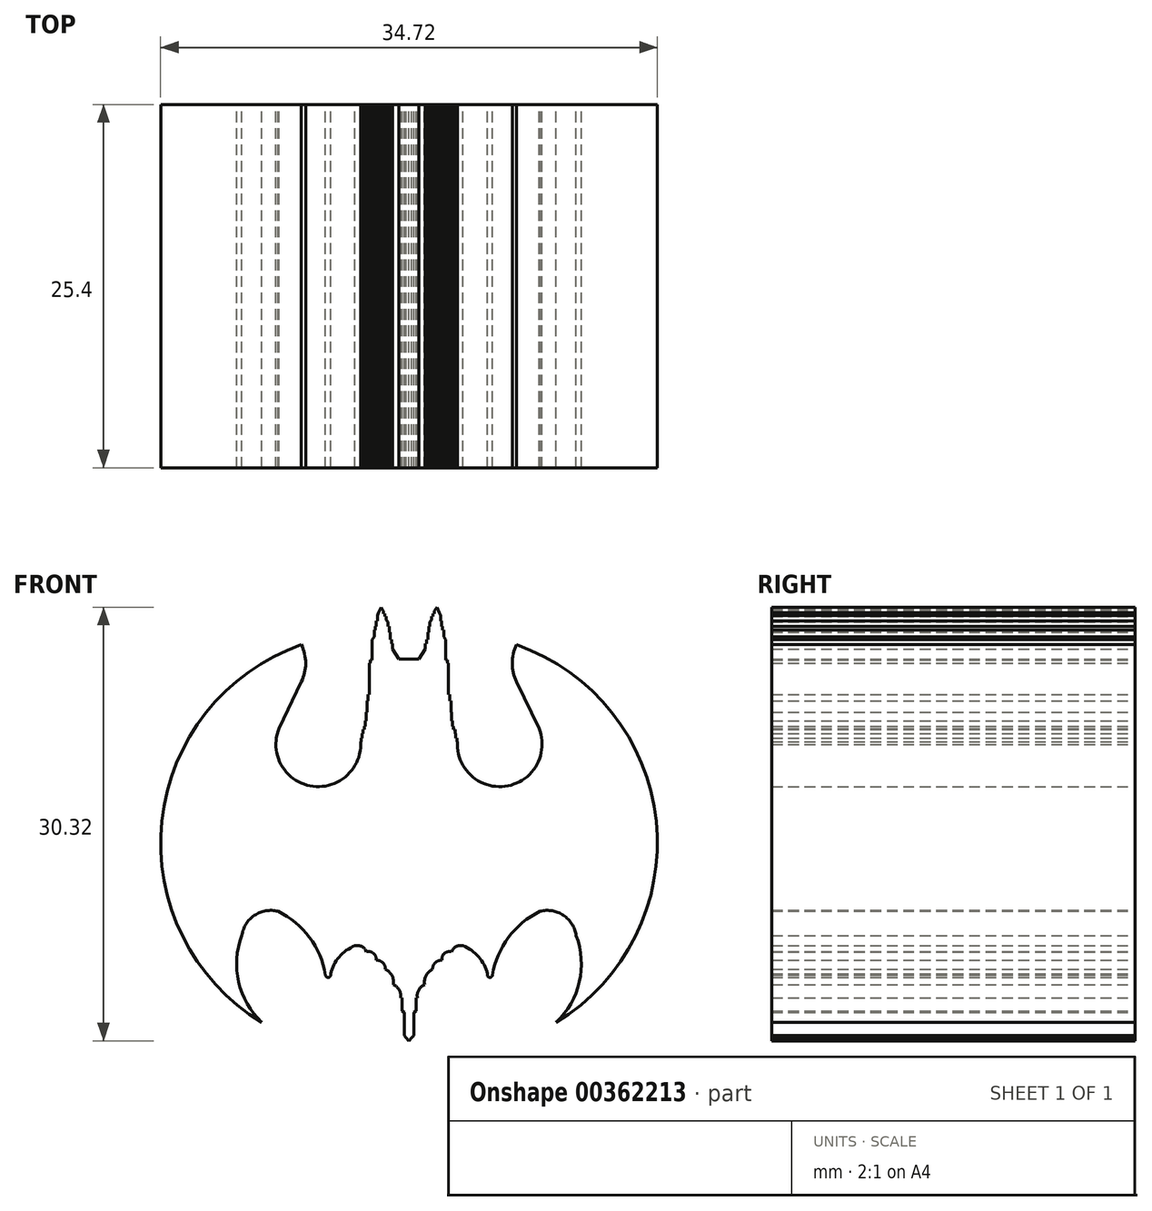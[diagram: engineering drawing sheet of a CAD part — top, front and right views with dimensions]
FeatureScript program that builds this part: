
annotation { "Feature Type Name" : "Feature", "Feature Type Description" : "" }
export const myFeature = defineFeature(function(context is Context, id is Id, definition is map)
    precondition{}
    {
        {
            var Q0;
            Q0=qCreatedBy(makeId("Front.planeOp"),FACE);
            var sketch = newSketch(context, id + "F0", { "sketchPlane" : qUnion([Q0])});
            skArc(sketch, "E0", {"start": v(10.29, -15.83) * mm, "mid": v(17.28, -1.75) * mm, "end": v(7.52, 10.57) * mm});
            skArc(sketch, "E1.MirrorCS", {"start": v(-10.29, -15.83) * mm, "mid": v(-17.28, -1.75) * mm, "end": v(-7.52, 10.57) * mm});
            skArc(sketch, "E2", {"start": v(-3.77, -10.48) * mm, "mid": v(-4.88, -11.25) * mm, "end": v(-5.48, -12.45) * mm});
            skArc(sketch, "E3", {"start": v(9.16, -8.07) * mm, "mid": v(6.96, -9.89) * mm, "end": v(5.84, -12.52) * mm});
            skArc(sketch, "E4", {"start": v(10.29, -15.83) * mm, "mid": v(11.91, -13) * mm, "end": v(11.68, -9.76) * mm});
            skArc(sketch, "E5.MirrorCS", {"start": v(3.77, -10.48) * mm, "mid": v(4.88, -11.25) * mm, "end": v(5.48, -12.45) * mm});
            skArc(sketch, "E6.MirrorCS", {"start": v(-9.16, -8.07) * mm, "mid": v(-6.96, -9.89) * mm, "end": v(-5.84, -12.52) * mm});
            skArc(sketch, "E7.MirrorCS", {"start": v(-10.29, -15.83) * mm, "mid": v(-11.91, -13) * mm, "end": v(-11.68, -9.76) * mm});
            skArc(sketch, "E8", {"start": v(11.68, -9.76) * mm, "mid": v(10.8, -8.35) * mm, "end": v(9.16, -8.07) * mm});
            skArc(sketch, "E9.MirrorCS", {"start": v(-11.68, -9.76) * mm, "mid": v(-10.8, -8.35) * mm, "end": v(-9.16, -8.07) * mm});
            skArc(sketch, "E10", {"start": v(-2.99, -10.9) * mm, "mid": v(-3.3, -10.53) * mm, "end": v(-3.77, -10.48) * mm});
            skArc(sketch, "E11", {"start": v(-2.3, -11.5) * mm, "mid": v(-2.48, -11) * mm, "end": v(-2.99, -10.9) * mm});
            skArc(sketch, "E12", {"start": v(-1.66, -12.13) * mm, "mid": v(-1.83, -11.66) * mm, "end": v(-2.3, -11.5) * mm});
            skArc(sketch, "E13", {"start": v(-1.1, -13.19) * mm, "mid": v(-1.19, -12.56) * mm, "end": v(-1.66, -12.13) * mm});
            skArc(sketch, "E14", {"start": v(-0.6, -14.12) * mm, "mid": v(-0.68, -13.56) * mm, "end": v(-1.1, -13.19) * mm});
            skLineSegment(sketch, "E15", {"start": v(-0.6, -14.12) * mm, "end": v(-0.48, -14.12) * mm});
            skLineSegment(sketch, "E16", {"start": v(-0.48, -14.12) * mm, "end": v(-0.48, -15.04) * mm});
            skLineSegment(sketch, "E17", {"start": v(-0.48, -15.04) * mm, "end": v(-0.34, -15.14) * mm});
            skLineSegment(sketch, "E18", {"start": v(-0.34, -15.14) * mm, "end": v(-0.34, -16.2) * mm});
            skLineSegment(sketch, "E19", {"start": v(-0.34, -16.2) * mm, "end": v(-0.34, -16.76) * mm});
            skLineSegment(sketch, "E20", {"start": v(-0.34, -16.76) * mm, "end": v(-0.2, -16.9) * mm});
            skLineSegment(sketch, "E21", {"start": v(-0.2, -16.9) * mm, "end": v(0, -17.12) * mm});
            skLineSegment(sketch, "E22", {"start": v(0, -17.12) * mm, "end": v(-0.2, -16.9) * mm});
            skArc(sketch, "E23.MirrorCS", {"start": v(2.99, -10.9) * mm, "mid": v(3.3, -10.53) * mm, "end": v(3.77, -10.48) * mm});
            skArc(sketch, "E24.MirrorCS", {"start": v(2.3, -11.5) * mm, "mid": v(2.48, -11) * mm, "end": v(2.99, -10.9) * mm});
            skArc(sketch, "E25.MirrorCS", {"start": v(1.66, -12.13) * mm, "mid": v(1.83, -11.66) * mm, "end": v(2.3, -11.5) * mm});
            skArc(sketch, "E26.MirrorCS", {"start": v(1.1, -13.19) * mm, "mid": v(1.19, -12.56) * mm, "end": v(1.66, -12.13) * mm});
            skArc(sketch, "E27.MirrorCS", {"start": v(0.6, -14.12) * mm, "mid": v(0.68, -13.56) * mm, "end": v(1.1, -13.19) * mm});
            skLineSegment(sketch, "E28.MirrorCS", {"start": v(0.48, -14.12) * mm, "end": v(0.48, -15.04) * mm});
            skLineSegment(sketch, "E29.MirrorCS", {"start": v(0.6, -14.12) * mm, "end": v(0.48, -14.12) * mm});
            skLineSegment(sketch, "E30.MirrorCS", {"start": v(0.34, -15.14) * mm, "end": v(0.34, -16.2) * mm});
            skLineSegment(sketch, "E31.MirrorCS", {"start": v(0.48, -15.04) * mm, "end": v(0.34, -15.14) * mm});
            skLineSegment(sketch, "E32.MirrorCS", {"start": v(0.34, -16.2) * mm, "end": v(0.34, -16.76) * mm});
            skLineSegment(sketch, "E33.MirrorCS", {"start": v(0.34, -16.76) * mm, "end": v(0.2, -16.9) * mm});
            skLineSegment(sketch, "E34.MirrorCS", {"start": v(0, -17.12) * mm, "end": v(0.2, -16.9) * mm});
            skArc(sketch, "E35", {"start": v(-5.84, -12.52) * mm, "mid": v(-5.62, -12.69) * mm, "end": v(-5.48, -12.45) * mm});
            skArc(sketch, "E36.MirrorCS", {"start": v(5.84, -12.52) * mm, "mid": v(5.62, -12.69) * mm, "end": v(5.48, -12.45) * mm});
            skArc(sketch, "E37", {"start": v(-7.52, 7.97) * mm, "mid": v(-7.23, 9.27) * mm, "end": v(-7.52, 10.57) * mm});
            skLineSegment(sketch, "E38", {"start": v(-7.52, 7.97) * mm, "end": v(-9.09, 4.72) * mm});
            skArc(sketch, "E39", {"start": v(-9.09, 4.72) * mm, "mid": v(-6.92, 0.7) * mm, "end": v(-3.38, 3.58) * mm});
            skLineSegment(sketch, "E40", {"start": v(-3.38, 3.58) * mm, "end": v(-3.38, 3.8) * mm});
            skLineSegment(sketch, "E41", {"start": v(-3.38, 3.8) * mm, "end": v(-3.34, 3.8) * mm});
            skLineSegment(sketch, "E42", {"start": v(-3.34, 3.8) * mm, "end": v(-3.34, 4.05) * mm});
            skLineSegment(sketch, "E43", {"start": v(-3.34, 4.05) * mm, "end": v(-3.27, 4.05) * mm});
            skLineSegment(sketch, "E44", {"start": v(-3.27, 4.05) * mm, "end": v(-3.27, 4.35) * mm});
            skLineSegment(sketch, "E45", {"start": v(-3.27, 4.35) * mm, "end": v(-3.22, 4.35) * mm});
            skLineSegment(sketch, "E46", {"start": v(-3.22, 4.35) * mm, "end": v(-3.22, 4.65) * mm});
            skLineSegment(sketch, "E47", {"start": v(-3.22, 4.65) * mm, "end": v(-3.11, 4.65) * mm});
            skLineSegment(sketch, "E48", {"start": v(-3.11, 4.65) * mm, "end": v(-3.11, 4.87) * mm});
            skLineSegment(sketch, "E49", {"start": v(-3.11, 4.87) * mm, "end": v(-3.05, 4.87) * mm});
            skLineSegment(sketch, "E50", {"start": v(-3.05, 4.87) * mm, "end": v(-3.05, 5.25) * mm});
            skLineSegment(sketch, "E51", {"start": v(-3.05, 5.25) * mm, "end": v(-2.98, 5.25) * mm});
            skLineSegment(sketch, "E52", {"start": v(-2.98, 5.25) * mm, "end": v(-2.98, 5.86) * mm});
            skLineSegment(sketch, "E53", {"start": v(-2.98, 5.86) * mm, "end": v(-2.94, 5.86) * mm});
            skLineSegment(sketch, "E54", {"start": v(-2.94, 5.86) * mm, "end": v(-2.94, 6.66) * mm});
            skLineSegment(sketch, "E55", {"start": v(-2.94, 6.66) * mm, "end": v(-2.86, 6.66) * mm});
            skLineSegment(sketch, "E56", {"start": v(-2.86, 6.66) * mm, "end": v(-2.86, 7.09) * mm});
            skLineSegment(sketch, "E57", {"start": v(-2.86, 7.09) * mm, "end": v(-2.77, 7.09) * mm});
            skLineSegment(sketch, "E58", {"start": v(-2.77, 7.09) * mm, "end": v(-2.77, 7.64) * mm});
            skLineSegment(sketch, "E59", {"start": v(-2.77, 7.64) * mm, "end": v(-2.77, 9.29) * mm});
            skLineSegment(sketch, "E60", {"start": v(-2.77, 9.29) * mm, "end": v(-2.7, 9.29) * mm});
            skLineSegment(sketch, "E61", {"start": v(-2.7, 9.29) * mm, "end": v(-2.7, 9.5) * mm});
            skLineSegment(sketch, "E62", {"start": v(-2.7, 9.5) * mm, "end": v(-2.56, 9.5) * mm});
            skLineSegment(sketch, "E63", {"start": v(-2.56, 9.5) * mm, "end": v(-2.56, 10.26) * mm});
            skLineSegment(sketch, "E64", {"start": v(-2.56, 10.26) * mm, "end": v(-2.56, 10.93) * mm});
            skLineSegment(sketch, "E65", {"start": v(-2.56, 10.93) * mm, "end": v(-2.42, 11.12) * mm});
            skLineSegment(sketch, "E66", {"start": v(-2.42, 11.12) * mm, "end": v(-2.42, 11.6) * mm});
            skLineSegment(sketch, "E67", {"start": v(-2.42, 11.6) * mm, "end": v(-2.35, 11.6) * mm});
            skLineSegment(sketch, "E68", {"start": v(-2.35, 11.6) * mm, "end": v(-2.35, 11.86) * mm});
            skLineSegment(sketch, "E69", {"start": v(-2.35, 11.86) * mm, "end": v(-2.28, 11.86) * mm});
            skLineSegment(sketch, "E70", {"start": v(-2.28, 11.86) * mm, "end": v(-2.28, 12.24) * mm});
            skLineSegment(sketch, "E71", {"start": v(-2.28, 12.24) * mm, "end": v(-2.2, 12.24) * mm});
            skLineSegment(sketch, "E72", {"start": v(-2.2, 12.24) * mm, "end": v(-2.2, 12.45) * mm});
            skLineSegment(sketch, "E73", {"start": v(-2.2, 12.45) * mm, "end": v(-2.2, 12.6) * mm});
            skLineSegment(sketch, "E74", {"start": v(-2.2, 12.6) * mm, "end": v(-2.13, 12.8) * mm});
            skLineSegment(sketch, "E75", {"start": v(-2.13, 12.8) * mm, "end": v(-1.95, 13.2) * mm});
            skLineSegment(sketch, "E76", {"start": v(-1.95, 13.2) * mm, "end": v(-1.88, 13.07) * mm});
            skLineSegment(sketch, "E77", {"start": v(-1.88, 13.07) * mm, "end": v(-1.79, 12.95) * mm});
            skLineSegment(sketch, "E78", {"start": v(-1.79, 12.95) * mm, "end": v(-1.79, 12.76) * mm});
            skLineSegment(sketch, "E79", {"start": v(-1.79, 12.76) * mm, "end": v(-1.69, 12.76) * mm});
            skLineSegment(sketch, "E80", {"start": v(-1.69, 12.76) * mm, "end": v(-1.69, 12.56) * mm});
            skLineSegment(sketch, "E81", {"start": v(-1.69, 12.56) * mm, "end": v(-1.59, 12.56) * mm});
            skLineSegment(sketch, "E82", {"start": v(-1.59, 12.56) * mm, "end": v(-1.59, 12.3) * mm});
            skLineSegment(sketch, "E83", {"start": v(-1.59, 12.3) * mm, "end": v(-1.46, 12.17) * mm});
            skLineSegment(sketch, "E84", {"start": v(-1.46, 12.17) * mm, "end": v(-1.46, 11.84) * mm});
            skLineSegment(sketch, "E85", {"start": v(-1.46, 11.84) * mm, "end": v(-1.38, 11.84) * mm});
            skLineSegment(sketch, "E86", {"start": v(-1.38, 11.84) * mm, "end": v(-1.38, 11.45) * mm});
            skLineSegment(sketch, "E87", {"start": v(-1.38, 11.45) * mm, "end": v(-1.32, 11.45) * mm});
            skLineSegment(sketch, "E88", {"start": v(-1.32, 11.45) * mm, "end": v(-1.32, 10.93) * mm});
            skLineSegment(sketch, "E89", {"start": v(-1.32, 10.93) * mm, "end": v(-1.23, 10.93) * mm});
            skLineSegment(sketch, "E90", {"start": v(-1.23, 10.93) * mm, "end": v(-1.23, 10.66) * mm});
            skLineSegment(sketch, "E91", {"start": v(-1.23, 10.66) * mm, "end": v(-1.15, 10.66) * mm});
            skLineSegment(sketch, "E92", {"start": v(-1.15, 10.66) * mm, "end": v(-1.15, 10.26) * mm});
            skLineSegment(sketch, "E93", {"start": v(-1.15, 10.26) * mm, "end": v(-0.7, 9.57) * mm});
            skLineSegment(sketch, "E94", {"start": v(-0.7, 9.57) * mm, "end": v(0, 9.57) * mm});
            skLineSegment(sketch, "E95", {"start": v(0, 9.57) * mm, "end": v(-0.7, 9.57) * mm});
            skArc(sketch, "E96.MirrorCS", {"start": v(9.09, 4.72) * mm, "mid": v(6.92, 0.7) * mm, "end": v(3.38, 3.58) * mm});
            skLineSegment(sketch, "E97.MirrorCS", {"start": v(3.38, 3.58) * mm, "end": v(3.38, 3.8) * mm});
            skLineSegment(sketch, "E98.MirrorCS", {"start": v(3.34, 3.8) * mm, "end": v(3.34, 4.05) * mm});
            skLineSegment(sketch, "E99.MirrorCS", {"start": v(3.38, 3.8) * mm, "end": v(3.34, 3.8) * mm});
            skLineSegment(sketch, "E100.MirrorCS", {"start": v(3.34, 4.05) * mm, "end": v(3.27, 4.05) * mm});
            skLineSegment(sketch, "E101.MirrorCS", {"start": v(3.27, 4.05) * mm, "end": v(3.27, 4.35) * mm});
            skLineSegment(sketch, "E102.MirrorCS", {"start": v(3.27, 4.35) * mm, "end": v(3.22, 4.35) * mm});
            skLineSegment(sketch, "E103.MirrorCS", {"start": v(3.22, 4.35) * mm, "end": v(3.22, 4.65) * mm});
            skLineSegment(sketch, "E104.MirrorCS", {"start": v(2.98, 5.25) * mm, "end": v(2.98, 5.86) * mm});
            skLineSegment(sketch, "E105.MirrorCS", {"start": v(2.94, 5.86) * mm, "end": v(2.94, 6.66) * mm});
            skLineSegment(sketch, "E106.MirrorCS", {"start": v(2.86, 6.66) * mm, "end": v(2.86, 7.09) * mm});
            skLineSegment(sketch, "E107.MirrorCS", {"start": v(2.77, 7.09) * mm, "end": v(2.77, 7.64) * mm});
            skLineSegment(sketch, "E108.MirrorCS", {"start": v(2.77, 7.64) * mm, "end": v(2.77, 9.29) * mm});
            skLineSegment(sketch, "E109.MirrorCS", {"start": v(2.86, 7.09) * mm, "end": v(2.77, 7.09) * mm});
            skLineSegment(sketch, "E110.MirrorCS", {"start": v(2.77, 9.29) * mm, "end": v(2.7, 9.29) * mm});
            skLineSegment(sketch, "E111.MirrorCS", {"start": v(2.7, 9.29) * mm, "end": v(2.7, 9.5) * mm});
            skLineSegment(sketch, "E112.MirrorCS", {"start": v(2.7, 9.5) * mm, "end": v(2.56, 9.5) * mm});
            skLineSegment(sketch, "E113.MirrorCS", {"start": v(2.56, 9.5) * mm, "end": v(2.56, 10.26) * mm});
            skLineSegment(sketch, "E114.MirrorCS", {"start": v(3.22, 4.65) * mm, "end": v(3.11, 4.65) * mm});
            skLineSegment(sketch, "E115.MirrorCS", {"start": v(3.11, 4.65) * mm, "end": v(3.11, 4.87) * mm});
            skLineSegment(sketch, "E116.MirrorCS", {"start": v(3.05, 4.87) * mm, "end": v(3.05, 5.25) * mm});
            skLineSegment(sketch, "E117.MirrorCS", {"start": v(3.11, 4.87) * mm, "end": v(3.05, 4.87) * mm});
            skLineSegment(sketch, "E118.MirrorCS", {"start": v(0, 9.57) * mm, "end": v(0.7, 9.57) * mm});
            skLineSegment(sketch, "E119.MirrorCS", {"start": v(1.15, 10.26) * mm, "end": v(0.7, 9.57) * mm});
            skLineSegment(sketch, "E120.MirrorCS", {"start": v(1.15, 10.66) * mm, "end": v(1.15, 10.26) * mm});
            skLineSegment(sketch, "E121.MirrorCS", {"start": v(1.23, 10.66) * mm, "end": v(1.15, 10.66) * mm});
            skLineSegment(sketch, "E122.MirrorCS", {"start": v(1.23, 10.93) * mm, "end": v(1.23, 10.66) * mm});
            skLineSegment(sketch, "E123.MirrorCS", {"start": v(1.32, 10.93) * mm, "end": v(1.23, 10.93) * mm});
            skLineSegment(sketch, "E124.MirrorCS", {"start": v(1.46, 12.17) * mm, "end": v(1.46, 11.84) * mm});
            skLineSegment(sketch, "E125.MirrorCS", {"start": v(1.38, 11.84) * mm, "end": v(1.38, 11.45) * mm});
            skLineSegment(sketch, "E126.MirrorCS", {"start": v(1.32, 11.45) * mm, "end": v(1.32, 10.93) * mm});
            skLineSegment(sketch, "E127.MirrorCS", {"start": v(1.38, 11.45) * mm, "end": v(1.32, 11.45) * mm});
            skLineSegment(sketch, "E128.MirrorCS", {"start": v(1.46, 11.84) * mm, "end": v(1.38, 11.84) * mm});
            skLineSegment(sketch, "E129.MirrorCS", {"start": v(1.59, 12.3) * mm, "end": v(1.46, 12.17) * mm});
            skLineSegment(sketch, "E130.MirrorCS", {"start": v(1.59, 12.56) * mm, "end": v(1.59, 12.3) * mm});
            skLineSegment(sketch, "E131.MirrorCS", {"start": v(1.69, 12.56) * mm, "end": v(1.59, 12.56) * mm});
            skLineSegment(sketch, "E132.MirrorCS", {"start": v(1.69, 12.76) * mm, "end": v(1.69, 12.56) * mm});
            skLineSegment(sketch, "E133.MirrorCS", {"start": v(1.79, 12.76) * mm, "end": v(1.69, 12.76) * mm});
            skLineSegment(sketch, "E134.MirrorCS", {"start": v(2.56, 10.26) * mm, "end": v(2.56, 10.93) * mm});
            skLineSegment(sketch, "E135.MirrorCS", {"start": v(2.56, 10.93) * mm, "end": v(2.42, 11.12) * mm});
            skLineSegment(sketch, "E136.MirrorCS", {"start": v(2.42, 11.12) * mm, "end": v(2.42, 11.6) * mm});
            skLineSegment(sketch, "E137.MirrorCS", {"start": v(2.35, 11.6) * mm, "end": v(2.35, 11.86) * mm});
            skLineSegment(sketch, "E138.MirrorCS", {"start": v(2.28, 11.86) * mm, "end": v(2.28, 12.24) * mm});
            skLineSegment(sketch, "E139.MirrorCS", {"start": v(2.2, 12.24) * mm, "end": v(2.2, 12.45) * mm});
            skLineSegment(sketch, "E140.MirrorCS", {"start": v(2.2, 12.6) * mm, "end": v(2.13, 12.8) * mm});
            skLineSegment(sketch, "E141.MirrorCS", {"start": v(2.13, 12.8) * mm, "end": v(1.95, 13.2) * mm});
            skLineSegment(sketch, "E142.MirrorCS", {"start": v(1.95, 13.2) * mm, "end": v(1.88, 13.07) * mm});
            skLineSegment(sketch, "E143.MirrorCS", {"start": v(1.88, 13.07) * mm, "end": v(1.79, 12.95) * mm});
            skLineSegment(sketch, "E144.MirrorCS", {"start": v(1.79, 12.95) * mm, "end": v(1.79, 12.76) * mm});
            skLineSegment(sketch, "E145.MirrorCS", {"start": v(2.35, 11.86) * mm, "end": v(2.28, 11.86) * mm});
            skLineSegment(sketch, "E146.MirrorCS", {"start": v(2.28, 12.24) * mm, "end": v(2.2, 12.24) * mm});
            skLineSegment(sketch, "E147.MirrorCS", {"start": v(2.2, 12.45) * mm, "end": v(2.2, 12.6) * mm});
            skLineSegment(sketch, "E148.MirrorCS", {"start": v(2.94, 6.66) * mm, "end": v(2.86, 6.66) * mm});
            skLineSegment(sketch, "E149.MirrorCS", {"start": v(3.05, 5.25) * mm, "end": v(2.98, 5.25) * mm});
            skLineSegment(sketch, "E150.MirrorCS", {"start": v(2.98, 5.86) * mm, "end": v(2.94, 5.86) * mm});
            skLineSegment(sketch, "E151.MirrorCS", {"start": v(7.52, 7.97) * mm, "end": v(9.09, 4.72) * mm});
            skArc(sketch, "E152.MirrorCS", {"start": v(7.52, 7.97) * mm, "mid": v(7.23, 9.27) * mm, "end": v(7.52, 10.57) * mm});
            skLineSegment(sketch, "E153.MirrorCS", {"start": v(2.42, 11.6) * mm, "end": v(2.35, 11.6) * mm});
            skSolve(sketch);
        }
        {
            var Q0;
            Q0 = qSketchRegion(id + "F0", true);
            extrude(context, id + "F1", {"entities" : qUnion([Q0]), "depth" : 25.4 * mm});
        }
    });
